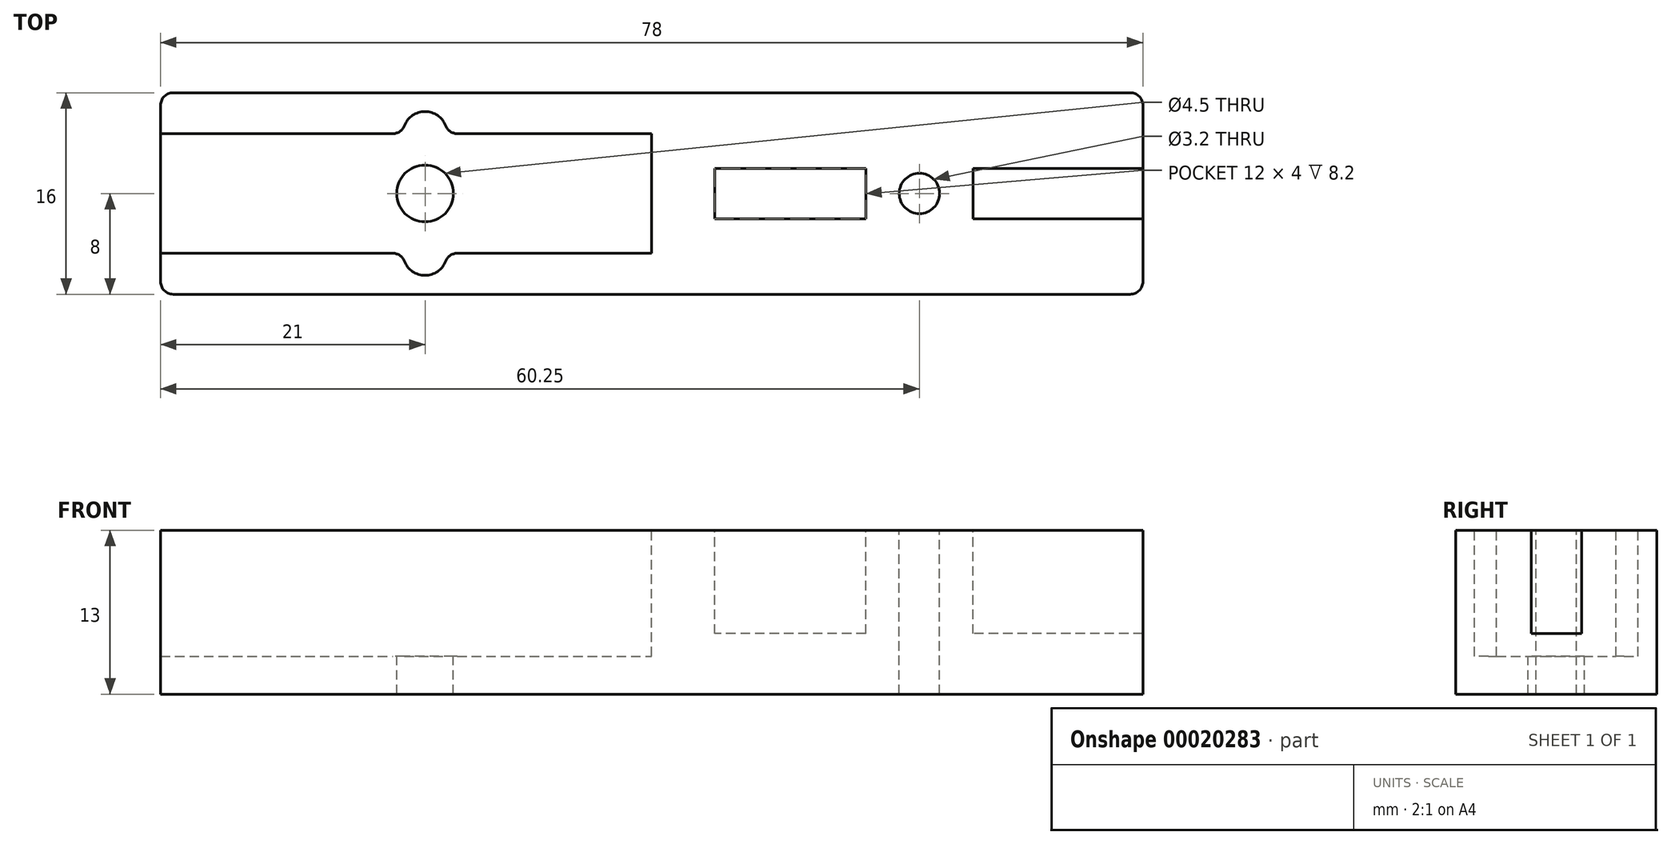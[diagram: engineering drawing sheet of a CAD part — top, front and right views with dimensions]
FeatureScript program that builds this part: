
annotation { "Feature Type Name" : "Feature", "Feature Type Description" : "" }
export const myFeature = defineFeature(function(context is Context, id is Id, definition is map)
    precondition{}
    {
        {
            var Q0;
            Q0=qCreatedBy(makeId("Top.planeOp"),FACE);
            var sketch = newSketch(context, id + "F0", { "sketchPlane" : qUnion([Q0])});
            skLineSegment(sketch, "E0.rect.bottom", {"start": v(39, -8) * mm, "end": v(-39, -8) * mm});
            skLineSegment(sketch, "E0.rect.top", {"start": v(39, 8) * mm, "end": v(-39, 8) * mm});
            skLineSegment(sketch, "E0.rect.left", {"start": v(39, -8) * mm, "end": v(39, 8) * mm});
            skLineSegment(sketch, "E0.rect.right", {"start": v(-39, -8) * mm, "end": v(-39, 8) * mm});
            skPoint(sketch, "E0.rect.middle", {"position": v(0, 0) * mm});
            skSolve(sketch);
        }
        {
            var Q0;
            Q0 = qSketchRegion(id + "F0", true);
            extrude(context, id + "F1", {"entities" : qUnion([Q0]), "depth" : 13 * mm});
        }
        {
            var Q0;
            Q0=makeQuery(id+"F1.opExtrude","CAP_FACE",FACE,{"disambiguationData":[OSD([sQuery(id+"F0.wireOp",EDGE,"E0.rect.bottom"),sQuery(id+"F0.wireOp",EDGE,"E0.rect.top"),sQuery(id+"F0.wireOp",EDGE,"E0.rect.left"),sQuery(id+"F0.wireOp",EDGE,"E0.rect.right")])],"isStart":false});
            var sketch = newSketch(context, id + "F2", { "sketchPlane" : qUnion([Q0])});
            skLineSegment(sketch, "E1.bottom", {"start": v(-39, 4.75) * mm, "end": v(-19.75, 4.75) * mm});
            skLineSegment(sketch, "E1.top", {"start": v(-39, -4.75) * mm, "end": v(-19.75, -4.75) * mm});
            skLineSegment(sketch, "E1.left", {"start": v(-39, 4.75) * mm, "end": v(-39, -4.75) * mm});
            skLineSegment(sketch, "E1.right", {"start": v(0, 4.75) * mm, "end": v(0, -4.75) * mm});
            skLineSegment(sketch, "E2", {"start": v(-39, 0) * mm, "end": v(0, -4.75) * mm, "construction": true});
            skLineSegment(sketch, "E3", {"start": v(0, 4.75) * mm, "end": v(-39, 0) * mm, "construction": true});
            skLineSegment(sketch, "E4", {"start": v(-18, 4.75) * mm, "end": v(-18, -4.75) * mm, "construction": true});
            skArc(sketch, "E5", {"start": v(-16.25, 4.75) * mm, "mid": v(-18, 6.5) * mm, "end": v(-19.75, 4.75) * mm});
            skArc(sketch, "E6", {"start": v(-19.75, -4.75) * mm, "mid": v(-18, -6.5) * mm, "end": v(-16.25, -4.75) * mm});
            skLineSegment(sketch, "E7.trimOffspring", {"start": v(-16.25, 4.75) * mm, "end": v(0, 4.75) * mm});
            skLineSegment(sketch, "E8.trimOffspring", {"start": v(-16.25, -4.75) * mm, "end": v(0, -4.75) * mm});
            skSolve(sketch);
        }
        {
            var Q0;
            Q0=makeQuery(id+"F2.imprint","IMPRINT",FACE,{"disambiguationData":[TD([[makeQuery(id+"F2.imprint","IMPRINT",EDGE,{"derivedFrom":sQuery(id+"F2.wireOp",EDGE,"E1.bottom")}),-1.0]])]});
            extrude(context, id + "F3", {"entities" : qUnion([Q0]), "operationType" : NewBodyOperationType.REMOVE, "oppositeDirection" : true, "depth" : 10 * mm});
        }
        {
            var Q0;
            Q0=makeQuery(id+"F3.boolean.opBoolean","COPY",FACE,{"derivedFrom":makeQuery(id+"F3.opExtrude","CAP_FACE",FACE,{"disambiguationData":[OSD([sQuery(id+"F2.wireOp",EDGE,"E1.bottom"),sQuery(id+"F2.wireOp",EDGE,"E1.top"),sQuery(id+"F2.wireOp",EDGE,"E1.left"),sQuery(id+"F2.wireOp",EDGE,"E1.right"),sQuery(id+"F2.wireOp",EDGE,"E5"),sQuery(id+"F2.wireOp",EDGE,"E6"),sQuery(id+"F2.wireOp",EDGE,"E7.trimOffspring"),sQuery(id+"F2.wireOp",EDGE,"E8.trimOffspring")])],"isStart":false})});
            var sketch = newSketch(context, id + "F4", { "sketchPlane" : qUnion([Q0])});
            skCircle(sketch, "E9", {"center": v(-18, 0) * mm, "radius": 2.25 * mm});
            skLineSegment(sketch, "E10", {"start": v(-18, 6.5) * mm, "end": v(-18, -6.5) * mm, "construction": true});
            skSolve(sketch);
        }
        {
            var Q0;
            Q0=makeQuery(id+"F4.imprint","IMPRINT",FACE,{"disambiguationData":[TD([[makeQuery(id+"F4.imprint","IMPRINT",EDGE,{"derivedFrom":sQuery(id+"F4.wireOp",EDGE,"E9")}),1.0]])]});
            var Q1;
            Q1=sQuery(id+"F4.wireOp",EDGE,"E9");
            extrude(context, id + "F5", {"entities" : qUnion([Q0]), "operationType" : NewBodyOperationType.REMOVE, "surfaceEntities" : qUnion([Q1]), "endBound" : BoundingType.THROUGH_ALL, "oppositeDirection" : true, "depth" : 25 * mm});
        }
        {
            var Q0;
            Q0=makeQuery(id+"F1.opExtrude","CAP_FACE",FACE,{"disambiguationData":[OSD([sQuery(id+"F0.wireOp",EDGE,"E0.rect.bottom"),sQuery(id+"F0.wireOp",EDGE,"E0.rect.top"),sQuery(id+"F0.wireOp",EDGE,"E0.rect.left"),sQuery(id+"F0.wireOp",EDGE,"E0.rect.right")])],"isStart":false});
            var sketch = newSketch(context, id + "F6", { "sketchPlane" : qUnion([Q0])});
            skLineSegment(sketch, "E11.bottom", {"start": v(39, 2) * mm, "end": v(25.5, 2) * mm});
            skLineSegment(sketch, "E11.top", {"start": v(39, -2) * mm, "end": v(25.5, -2) * mm});
            skLineSegment(sketch, "E11.left", {"start": v(39, 2) * mm, "end": v(39, -2) * mm});
            skLineSegment(sketch, "E11.right", {"start": v(25.5, 2) * mm, "end": v(25.5, -2) * mm});
            skLineSegment(sketch, "E12.bottom", {"start": v(17, 2) * mm, "end": v(5, 2) * mm});
            skLineSegment(sketch, "E12.top", {"start": v(17, -2) * mm, "end": v(5, -2) * mm});
            skLineSegment(sketch, "E12.left", {"start": v(17, 2) * mm, "end": v(17, -2) * mm});
            skLineSegment(sketch, "E12.right", {"start": v(5, 2) * mm, "end": v(5, -2) * mm});
            skLineSegment(sketch, "E13", {"start": v(25.5, -2) * mm, "end": v(39, -8) * mm, "construction": true});
            skLineSegment(sketch, "E14", {"start": v(25.5, 2) * mm, "end": v(39, 8) * mm, "construction": true});
            skSolve(sketch);
        }
        {
            var Q0;
            Q0=makeQuery(id+"F6.imprint","IMPRINT",FACE,{"disambiguationData":[TD([[makeQuery(id+"F6.imprint","IMPRINT",EDGE,{"derivedFrom":sQuery(id+"F6.wireOp",EDGE,"E12.bottom")}),1.0]])]});
            var Q1;
            Q1=makeQuery(id+"F6.imprint","IMPRINT",FACE,{"disambiguationData":[TD([[makeQuery(id+"F6.imprint","IMPRINT",EDGE,{"derivedFrom":sQuery(id+"F6.wireOp",EDGE,"E11.bottom")}),1.0]])]});
            extrude(context, id + "F7", {"entities" : qUnion([Q0, Q1]), "operationType" : NewBodyOperationType.REMOVE, "oppositeDirection" : true, "depth" : 8.2 * mm});
        }
        {
            var Q0;
            Q0=makeQuery(id+"F1.opExtrude","CAP_FACE",FACE,{"disambiguationData":[OSD([sQuery(id+"F0.wireOp",EDGE,"E0.rect.bottom"),sQuery(id+"F0.wireOp",EDGE,"E0.rect.top"),sQuery(id+"F0.wireOp",EDGE,"E0.rect.left"),sQuery(id+"F0.wireOp",EDGE,"E0.rect.right")])],"isStart":false});
            var sketch = newSketch(context, id + "F8", { "sketchPlane" : qUnion([Q0])});
            skCircle(sketch, "E15", {"center": v(21.25, 0) * mm, "radius": 1.6 * mm});
            skLineSegment(sketch, "E16", {"start": v(17, 0) * mm, "end": v(25.5, 0) * mm, "construction": true});
            skSolve(sketch);
        }
        {
            var Q0;
            Q0=makeQuery(id+"F8.imprint","IMPRINT",FACE,{"disambiguationData":[TD([[makeQuery(id+"F8.imprint","IMPRINT",EDGE,{"derivedFrom":sQuery(id+"F8.wireOp",EDGE,"E15")}),1.0]])]});
            var Q1;
            Q1=sQuery(id+"F8.wireOp",EDGE,"E16");
            extrude(context, id + "F9", {"entities" : qUnion([Q0]), "operationType" : NewBodyOperationType.REMOVE, "surfaceEntities" : qUnion([Q1]), "endBound" : BoundingType.THROUGH_ALL, "oppositeDirection" : true, "depth" : 25 * mm});
        }
        {
            var Q0;
            Q0=makeQuery(id+"F3.boolean.opBoolean","COPY",EDGE,{"derivedFrom":makeQuery(id+"F3.opExtrude","SWEPT_EDGE",EDGE,{"disambiguationData":[OSD([sQuery(id+"F2.wireOp",EDGE,"E5"),sQuery(id+"F2.wireOp",EDGE,"E7.trimOffspring")])]})});
            var Q1;
            Q1=makeQuery(id+"F3.boolean.opBoolean","COPY",EDGE,{"derivedFrom":makeQuery(id+"F3.opExtrude","SWEPT_EDGE",EDGE,{"disambiguationData":[OSD([sQuery(id+"F2.wireOp",EDGE,"E1.bottom"),sQuery(id+"F2.wireOp",EDGE,"E5")])]})});
            var Q2;
            Q2=makeQuery(id+"F3.boolean.opBoolean","COPY",EDGE,{"derivedFrom":makeQuery(id+"F3.opExtrude","SWEPT_EDGE",EDGE,{"disambiguationData":[OSD([sQuery(id+"F2.wireOp",EDGE,"E6"),sQuery(id+"F2.wireOp",EDGE,"E8.trimOffspring")])]})});
            var Q3;
            Q3=makeQuery(id+"F3.boolean.opBoolean","COPY",EDGE,{"derivedFrom":makeQuery(id+"F3.opExtrude","SWEPT_EDGE",EDGE,{"disambiguationData":[OSD([sQuery(id+"F2.wireOp",EDGE,"E1.top"),sQuery(id+"F2.wireOp",EDGE,"E6")])]})});
            var Q4;
            Q4=makeQuery(id+"F1.opExtrude","SWEPT_EDGE",EDGE,{"disambiguationData":[OSD([sQuery(id+"F0.wireOp",EDGE,"E0.rect.top"),sQuery(id+"F0.wireOp",EDGE,"E0.rect.right")])]});
            var Q5;
            Q5=makeQuery(id+"F1.opExtrude","SWEPT_EDGE",EDGE,{"disambiguationData":[OSD([sQuery(id+"F0.wireOp",EDGE,"E0.rect.bottom"),sQuery(id+"F0.wireOp",EDGE,"E0.rect.right")])]});
            var Q6;
            Q6=makeQuery(id+"F1.opExtrude","SWEPT_EDGE",EDGE,{"disambiguationData":[OSD([sQuery(id+"F0.wireOp",EDGE,"E0.rect.bottom"),sQuery(id+"F0.wireOp",EDGE,"E0.rect.left")])]});
            var Q7;
            Q7=makeQuery(id+"F1.opExtrude","SWEPT_EDGE",EDGE,{"disambiguationData":[OSD([sQuery(id+"F0.wireOp",EDGE,"E0.rect.top"),sQuery(id+"F0.wireOp",EDGE,"E0.rect.left")])]});
            var Q8;
            Q8=makeQuery(id+"F3.boolean.opBoolean","COPY",EDGE,{"derivedFrom":makeQuery(id+"F3.opExtrude","CAP_EDGE",EDGE,{"disambiguationData":[OSD([sQuery(id+"F2.wireOp",EDGE,"E7.trimOffspring")])],"isStart":true})});
            var Q9;
            Q9=makeQuery(id+"F3.boolean.opBoolean","COPY",EDGE,{"derivedFrom":makeQuery(id+"F3.opExtrude","CAP_EDGE",EDGE,{"disambiguationData":[OSD([sQuery(id+"F2.wireOp",EDGE,"E1.bottom")])],"isStart":true})});
            var Q10;
            Q10=makeQuery(id+"F3.boolean.opBoolean","COPY",EDGE,{"derivedFrom":makeQuery(id+"F3.opExtrude","CAP_EDGE",EDGE,{"disambiguationData":[OSD([sQuery(id+"F2.wireOp",EDGE,"E5")])],"isStart":true})});
            var Q11;
            Q11=makeQuery(id+"F3.boolean.opBoolean","COPY",EDGE,{"derivedFrom":makeQuery(id+"F3.opExtrude","CAP_EDGE",EDGE,{"disambiguationData":[OSD([sQuery(id+"F2.wireOp",EDGE,"E8.trimOffspring")])],"isStart":true})});
            var Q12;
            Q12=makeQuery(id+"F3.boolean.opBoolean","COPY",EDGE,{"derivedFrom":makeQuery(id+"F3.opExtrude","CAP_EDGE",EDGE,{"disambiguationData":[OSD([sQuery(id+"F2.wireOp",EDGE,"E6")])],"isStart":true})});
            var Q13;
            Q13=makeQuery(id+"F3.boolean.opBoolean","COPY",EDGE,{"derivedFrom":makeQuery(id+"F3.opExtrude","CAP_EDGE",EDGE,{"disambiguationData":[OSD([sQuery(id+"F2.wireOp",EDGE,"E1.top")])],"isStart":true})});
            var Q14;
            Q14=makeQuery(id+"F3.boolean.opBoolean","COPY",EDGE,{"derivedFrom":makeQuery(id+"F3.opExtrude","CAP_EDGE",EDGE,{"disambiguationData":[OSD([sQuery(id+"F2.wireOp",EDGE,"E1.right")])],"isStart":true})});
            var Q15;
            Q15=makeQuery(id+"F7.boolean.opBoolean","COPY",EDGE,{"derivedFrom":makeQuery(id+"F7.opExtrude","CAP_EDGE",EDGE,{"disambiguationData":[OSD([sQuery(id+"F6.wireOp",EDGE,"E12.top")])],"isStart":true})});
            var Q16;
            Q16=makeQuery(id+"F7.boolean.opBoolean","COPY",EDGE,{"derivedFrom":makeQuery(id+"F7.opExtrude","CAP_EDGE",EDGE,{"disambiguationData":[OSD([sQuery(id+"F6.wireOp",EDGE,"E12.left")])],"isStart":true})});
            var Q17;
            Q17=makeQuery(id+"F7.boolean.opBoolean","COPY",EDGE,{"derivedFrom":makeQuery(id+"F7.opExtrude","CAP_EDGE",EDGE,{"disambiguationData":[OSD([sQuery(id+"F6.wireOp",EDGE,"E12.bottom")])],"isStart":true})});
            var Q18;
            Q18=makeQuery(id+"F7.boolean.opBoolean","COPY",EDGE,{"derivedFrom":makeQuery(id+"F7.opExtrude","CAP_EDGE",EDGE,{"disambiguationData":[OSD([sQuery(id+"F6.wireOp",EDGE,"E12.right")])],"isStart":true})});
            var Q19;
            Q19=makeQuery(id+"F7.boolean.opBoolean","COPY",EDGE,{"derivedFrom":makeQuery(id+"F7.opExtrude","CAP_EDGE",EDGE,{"disambiguationData":[OSD([sQuery(id+"F6.wireOp",EDGE,"E11.right")])],"isStart":true})});
            var Q20;
            Q20=makeQuery(id+"F7.boolean.opBoolean","COPY",EDGE,{"derivedFrom":makeQuery(id+"F7.opExtrude","CAP_EDGE",EDGE,{"disambiguationData":[OSD([sQuery(id+"F6.wireOp",EDGE,"E11.bottom")])],"isStart":true})});
            var Q21;
            Q21=makeQuery(id+"F7.boolean.opBoolean","COPY",EDGE,{"derivedFrom":makeQuery(id+"F7.opExtrude","CAP_EDGE",EDGE,{"disambiguationData":[OSD([sQuery(id+"F6.wireOp",EDGE,"E11.top")])],"isStart":true})});
            var Q22;
            Q22=makeQuery(id+"F7.boolean.opBoolean","COPY",EDGE,{"derivedFrom":makeQuery(id+"F7.opExtrude","SWEPT_EDGE",EDGE,{"disambiguationData":[OSD([sQuery(id+"F0.wireOp",EDGE,"E0.rect.left"),sQuery(id+"F6.wireOp",EDGE,"E11.top"),sQuery(id+"F6.wireOp",EDGE,"E11.left")])]})});
            var Q23;
            Q23=makeQuery(id+"F7.boolean.opBoolean","COPY",EDGE,{"derivedFrom":makeQuery(id+"F7.opExtrude","SWEPT_EDGE",EDGE,{"disambiguationData":[OSD([sQuery(id+"F0.wireOp",EDGE,"E0.rect.left"),sQuery(id+"F6.wireOp",EDGE,"E11.bottom"),sQuery(id+"F6.wireOp",EDGE,"E11.left")])]})});
            fillet(context, id + "F10", {"entities" : qUnion([Q0, Q1, Q2, Q3, Q4, Q5, Q6, Q7, Q8, Q9, Q10, Q11, Q12, Q13, Q14, Q15, Q16, Q17, Q18, Q19, Q20, Q21, Q22, Q23]), "radius" : 1 * mm, "tangentPropagation" : true, "allowEdgeOverflow" : false});
        }
    });
